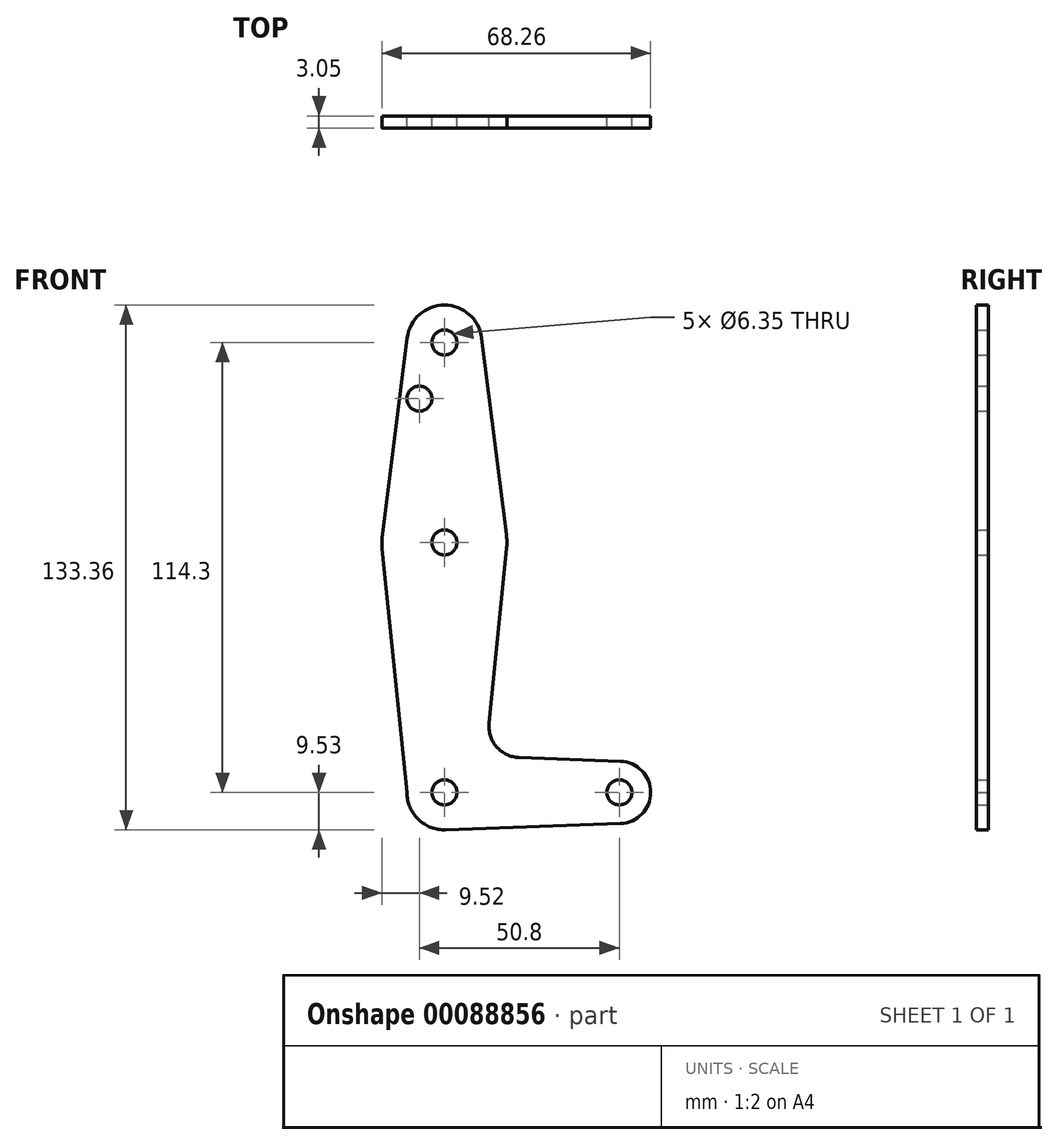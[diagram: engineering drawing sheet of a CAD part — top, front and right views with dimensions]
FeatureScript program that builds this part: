
annotation { "Feature Type Name" : "Feature", "Feature Type Description" : "" }
export const myFeature = defineFeature(function(context is Context, id is Id, definition is map)
    precondition{}
    {
        {
            var Q0;
            Q0=qCreatedBy(makeId("Front.planeOp"),FACE);
            var sketch = newSketch(context, id + "F0", { "sketchPlane" : qUnion([Q0])});
            skCircle(sketch, "E0", {"center": v(0, 114.3) * mm, "radius": 9.52 * mm});
            skCircle(sketch, "E1", {"center": v(0, 63.5) * mm, "radius": 15.88 * mm});
            skCircle(sketch, "E2", {"center": v(0, 0) * mm, "radius": 9.52 * mm});
            skLineSegment(sketch, "E3", {"start": v(0, 0) * mm, "end": v(44.45, 0) * mm, "construction": true});
            skLineSegment(sketch, "E4", {"start": v(-9.53, 0) * mm, "end": v(-15.8, 61.9) * mm});
            skLineSegment(sketch, "E5", {"start": v(-15.75, 65.48) * mm, "end": v(-9.45, 115.5) * mm});
            skLineSegment(sketch, "E6", {"start": v(15.75, 65.48) * mm, "end": v(9.45, 115.5) * mm});
            skCircle(sketch, "E7", {"center": v(0, 114.3) * mm, "radius": 3.18 * mm});
            skCircle(sketch, "E8", {"center": v(0, 0) * mm, "radius": 3.18 * mm});
            skCircle(sketch, "E9", {"center": v(0, 63.5) * mm, "radius": 3.18 * mm});
            skCircle(sketch, "E10", {"center": v(-6.35, 100.03) * mm, "radius": 3.18 * mm});
            skCircle(sketch, "E11", {"center": v(44.45, 0) * mm, "radius": 3.18 * mm});
            skCircle(sketch, "E12", {"center": v(44.45, 0) * mm, "radius": 7.94 * mm});
            skLineSegment(sketch, "E13", {"start": v(15.8, 61.91) * mm, "end": v(11.34, 17.6) * mm});
            skLineSegment(sketch, "E14", {"start": v(0.34, -9.52) * mm, "end": v(44.73, -7.93) * mm});
            skLineSegment(sketch, "E15", {"start": v(18.97, 8.85) * mm, "end": v(44.73, 7.93) * mm});
            skArc(sketch, "E16.filletArc", {"start": v(11.34, 17.6) * mm, "mid": v(13.26, 11.57) * mm, "end": v(18.97, 8.85) * mm});
            skLineSegment(sketch, "E17", {"start": v(0, 114.3) * mm, "end": v(0, 0) * mm});
            skSolve(sketch);
        }
        {
            var Q0;
            Q0 = qSketchRegion(id + "F0", true);
            extrude(context, id + "F1", {"entities" : qUnion([Q0]), "depth" : 3.05 * mm});
        }
    });
